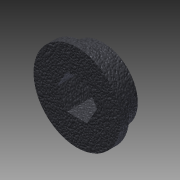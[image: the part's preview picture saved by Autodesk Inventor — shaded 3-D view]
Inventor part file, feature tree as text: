
AUTODESK INVENTOR PART (.ipt)
format: ipt  version: 2014 SP1 (Build 180222100, 222)  size: 111,104 bytes
history: native  units: in
note: dims shown in document units (in); Inventor stores cm internally (conversion verified against a paired STEP export)
features: extrude x4, sketch x4
ambient origin geometry x8: Origin, YZ Plane, XZ Plane, XY Plane, X Axis, Y Axis, Z Axis, Center Point
bodies: Solid1 (feature_tree)
feature tree (8):
  extrude  "Extrusion1"  Depth=0.25in TaperAngle=0.0deg
  extrude  "Extrusion2"  Depth=0.125in TaperAngle=0.0deg
  extrude  "Extrusion3"  Depth=0.5in
  extrude  "Extrusion4"  [1 undecoded]
  sketch  "Sketch1"  dims[d0=1.0in d1=0.25in d2=0.0in]
  sketch  "Sketch2"  dims[d3=1.25in d4=0.125in d5=0.0in]
  sketch  "Sketch3"  dims[d6=0.125in d7=0.0in d8=0.5in]
  sketch  "Sketch4"  dims[d9=0.125in d10=0.0in]
note: 1 required parameter value undecoded (feature->parameter linkage not recoverable at this tier; creation-order binding heuristic only, values carry confidence <= 0.55)
